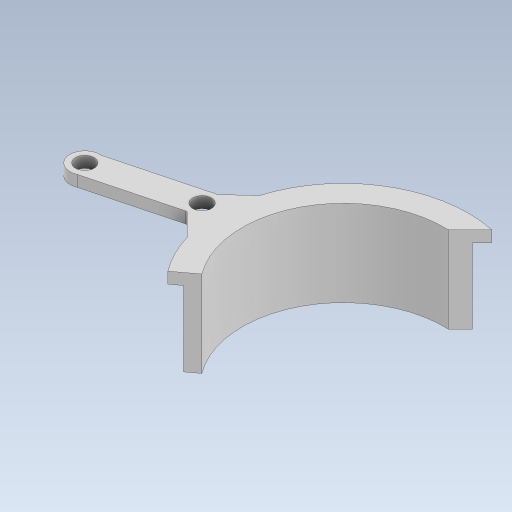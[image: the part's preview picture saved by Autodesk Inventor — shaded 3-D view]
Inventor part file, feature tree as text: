
AUTODESK INVENTOR PART (.ipt)
format: ipt  version: 2023.5 (Build 275446000, 446)  size: 342,528 bytes
history: native  units: mm
features: extrude x2, sketch x1
ambient origin geometry x8: Origin, YZ Plane, XZ Plane, XY Plane, X Axis, Y Axis, Z Axis, Center Point
bodies: Solid1 (feature_tree)
feature tree (3):
  sketch  "Sketch1"  dims[d8=3.0mm d9=0.0mm d10=3.0mm d11=0.0mm d14=135.0deg d15=20.0mm d16=0.0mm d17=25.0mm d18=67.0mm d19=61.0mm d20=58.0mm d21=8.0mm d22=5.0mm d23=8.0mm d24=5.0mm d25=19.0mm d27=54.0mm d28=20.0mm d29=45.0deg d26=0.5mm]
  extrude  "Extrusion1"  Depth=3.0mm TaperAngle=0.0deg
  extrude  "Extrusion2"  TaperAngle=135.0deg  [1 undecoded]
note: 1 required parameter value undecoded (feature->parameter linkage not recoverable at this tier; creation-order binding heuristic only, values carry confidence <= 0.55)
